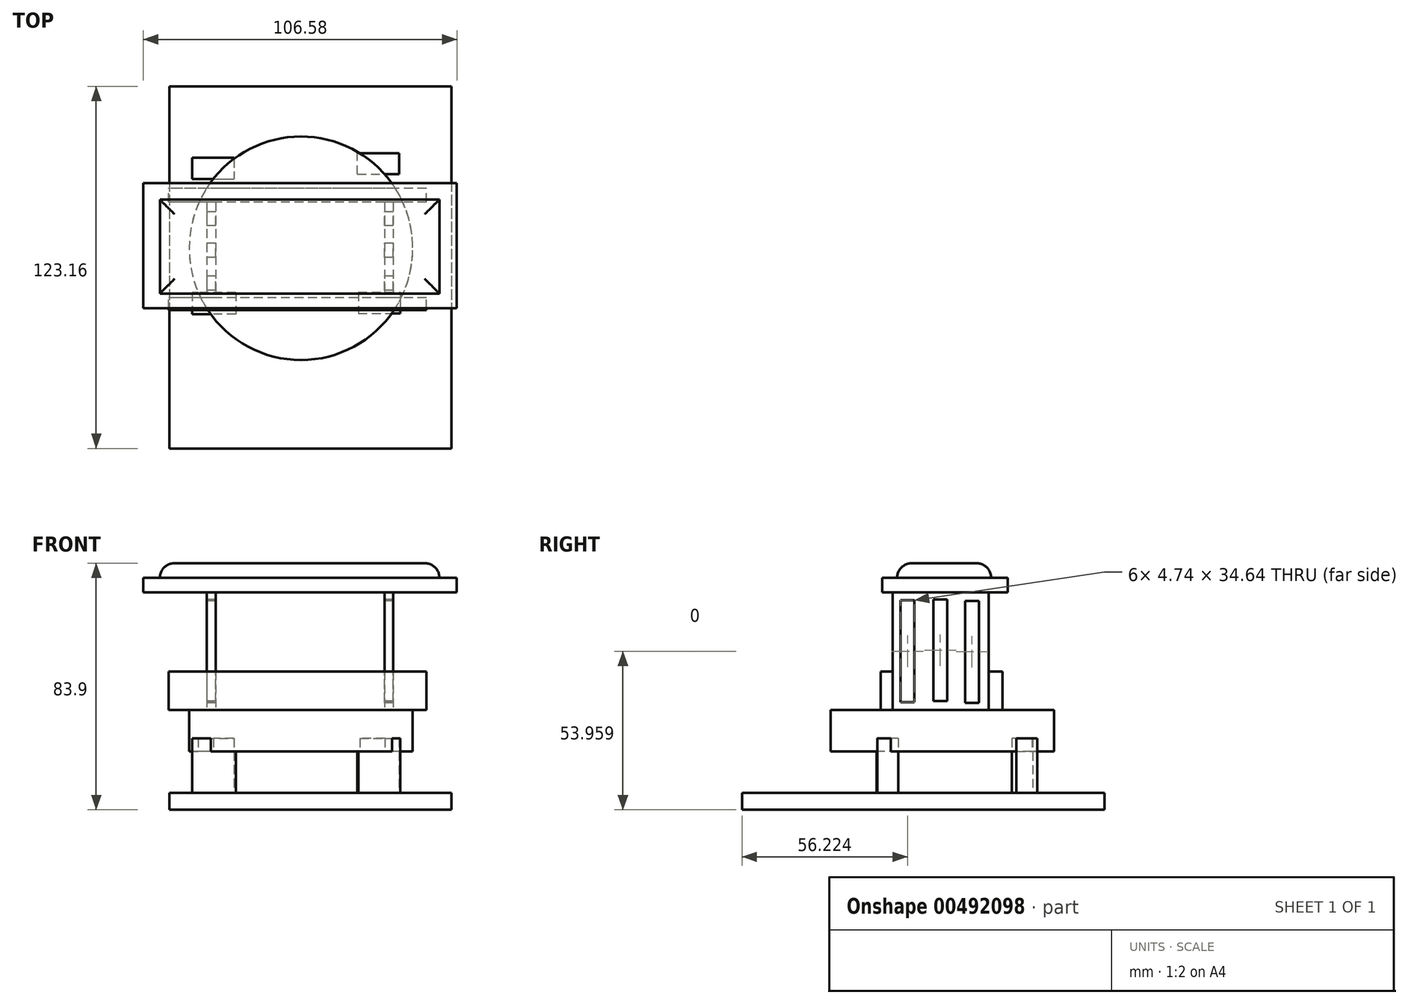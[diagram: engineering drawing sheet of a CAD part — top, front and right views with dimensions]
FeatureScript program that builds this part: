
annotation { "Feature Type Name" : "Feature", "Feature Type Description" : "" }
export const myFeature = defineFeature(function(context is Context, id is Id, definition is map)
    precondition{}
    {
        {
            var Q0;
            Q0=qCreatedBy(makeId("Top.planeOp"),FACE);
            var sketch = newSketch(context, id + "F0", { "sketchPlane" : qUnion([Q0])});
            skLineSegment(sketch, "E0.bottom", {"start": v(-47.96, 61.58) * mm, "end": v(47.96, 61.58) * mm});
            skLineSegment(sketch, "E0.top", {"start": v(-47.96, -61.58) * mm, "end": v(47.96, -61.58) * mm});
            skLineSegment(sketch, "E0.left", {"start": v(-47.96, 61.58) * mm, "end": v(-47.96, -61.58) * mm});
            skLineSegment(sketch, "E0.right", {"start": v(47.96, 61.58) * mm, "end": v(47.96, -61.58) * mm});
            skPoint(sketch, "E0.middle", {"position": v(0, 0) * mm});
            skSolve(sketch);
        }
        {
            var Q0;
            Q0=makeQuery(id+"F0.imprint","IMPRINT",FACE,{"disambiguationData":[TD([[makeQuery(id+"F0.imprint","IMPRINT",EDGE,{"derivedFrom":sQuery(id+"F0.wireOp",EDGE,"E0.bottom")}),-1.0]])]});
            extrude(context, id + "F1", {"entities" : qUnion([Q0]), "depth" : 5.8 * mm});
        }
        {
            var Q0;
            Q0=makeQuery(id+"F1.opExtrude","CAP_FACE",FACE,{"disambiguationData":[OSD([sQuery(id+"F0.wireOp",EDGE,"E0.bottom"),sQuery(id+"F0.wireOp",EDGE,"E0.top"),sQuery(id+"F0.wireOp",EDGE,"E0.left"),sQuery(id+"F0.wireOp",EDGE,"E0.right")])],"isStart":false});
            var sketch = newSketch(context, id + "F2", { "sketchPlane" : qUnion([Q0])});
            skLineSegment(sketch, "E1.bottom", {"start": v(-25.44, -8.5) * mm, "end": v(-40.27, -8.5) * mm});
            skLineSegment(sketch, "E1.top", {"start": v(-25.44, -15.91) * mm, "end": v(-40.27, -15.91) * mm});
            skLineSegment(sketch, "E1.left", {"start": v(-25.44, -8.5) * mm, "end": v(-25.44, -15.91) * mm});
            skLineSegment(sketch, "E1.right", {"start": v(-40.27, -8.5) * mm, "end": v(-40.27, -15.91) * mm});
            skPoint(sketch, "E1.middle", {"position": v(-32.86, -12.2) * mm});
            skLineSegment(sketch, "E2.bottom", {"start": v(-40.27, 37.26) * mm, "end": v(-26.06, 37.26) * mm});
            skLineSegment(sketch, "E2.top", {"start": v(-40.27, 30.12) * mm, "end": v(-26.06, 30.12) * mm});
            skLineSegment(sketch, "E2.left", {"start": v(-40.27, 37.26) * mm, "end": v(-40.27, 30.12) * mm});
            skLineSegment(sketch, "E2.right", {"start": v(-26.06, 37.26) * mm, "end": v(-26.06, 30.12) * mm});
            skPoint(sketch, "E2.middle", {"position": v(-33.17, 33.7) * mm});
            skLineSegment(sketch, "E3.bottom", {"start": v(15.96, 31.67) * mm, "end": v(30.17, 31.67) * mm});
            skLineSegment(sketch, "E3.top", {"start": v(15.96, 38.8) * mm, "end": v(30.17, 38.8) * mm});
            skLineSegment(sketch, "E3.left", {"start": v(15.96, 31.67) * mm, "end": v(15.96, 38.8) * mm});
            skLineSegment(sketch, "E3.right", {"start": v(30.17, 31.67) * mm, "end": v(30.17, 38.8) * mm});
            skPoint(sketch, "E3.middle", {"position": v(23.06, 35.24) * mm});
            skLineSegment(sketch, "E4.bottom", {"start": v(16.26, -8.46) * mm, "end": v(30.48, -8.46) * mm});
            skLineSegment(sketch, "E4.top", {"start": v(16.26, -15.6) * mm, "end": v(30.48, -15.6) * mm});
            skLineSegment(sketch, "E4.left", {"start": v(16.26, -8.46) * mm, "end": v(16.26, -15.6) * mm});
            skLineSegment(sketch, "E4.right", {"start": v(30.48, -8.46) * mm, "end": v(30.48, -15.6) * mm});
            skPoint(sketch, "E4.middle", {"position": v(23.37, -12.03) * mm});
            skSolve(sketch);
        }
        {
            var Q0;
            Q0=makeQuery(id+"F2.imprint","IMPRINT",FACE,{"disambiguationData":[TD([[makeQuery(id+"F2.imprint","IMPRINT",EDGE,{"derivedFrom":sQuery(id+"F2.wireOp",EDGE,"E2.bottom")}),-1.0]])]});
            var Q1;
            Q1=makeQuery(id+"F2.imprint","IMPRINT",FACE,{"disambiguationData":[TD([[makeQuery(id+"F2.imprint","IMPRINT",EDGE,{"derivedFrom":sQuery(id+"F2.wireOp",EDGE,"E3.bottom")}),1.0]])]});
            var Q2;
            Q2=makeQuery(id+"F2.imprint","IMPRINT",FACE,{"disambiguationData":[TD([[makeQuery(id+"F2.imprint","IMPRINT",EDGE,{"derivedFrom":sQuery(id+"F2.wireOp",EDGE,"E4.bottom")}),-1.0]])]});
            var Q3;
            Q3=makeQuery(id+"F2.imprint","IMPRINT",FACE,{"disambiguationData":[TD([[makeQuery(id+"F2.imprint","IMPRINT",EDGE,{"derivedFrom":sQuery(id+"F2.wireOp",EDGE,"E1.bottom")}),1.0]])]});
            extrude(context, id + "F3", {"entities" : qUnion([Q0, Q1, Q2, Q3]), "operationType" : NewBodyOperationType.ADD, "depth" : 18.5 * mm});
        }
        {
            var Q0;
            Q0=makeQuery(id+"F3.opExtrude","CAP_FACE",FACE,{"disambiguationData":[OSD([sQuery(id+"F2.wireOp",EDGE,"E2.bottom"),sQuery(id+"F2.wireOp",EDGE,"E2.top"),sQuery(id+"F2.wireOp",EDGE,"E2.left"),sQuery(id+"F2.wireOp",EDGE,"E2.right")])],"isStart":false});
            cPlane(context, id + "F4", {"entities" : qUnion([Q0]), "cplaneType" : CPlaneType.OFFSET, "offset" : 4.4 * mm, "oppositeDirection" : true, "width" : 150 * mm, "height" : 150 * mm});
        }
        {
            var Q0;
            Q0=qCreatedBy(id+"F4.planeOp",FACE);
            var sketch = newSketch(context, id + "F5", { "sketchPlane" : qUnion([Q0])});
            skCircle(sketch, "E5", {"center": v(-3.26, 6.51) * mm, "radius": 38 * mm});
            skSolve(sketch);
        }
        {
            var Q0;
            Q0 = qSketchRegion(id + "F5", true);
            extrude(context, id + "F6", {"entities" : qUnion([Q0]), "operationType" : NewBodyOperationType.ADD, "depth" : 14 * mm});
        }
        {
            var Q0;
            Q0=makeQuery(id+"F6.opExtrude","CAP_FACE",FACE,{"disambiguationData":[OSD([sQuery(id+"F5.wireOp",EDGE,"E5")])],"isStart":false});
            var sketch = newSketch(context, id + "F7", { "sketchPlane" : qUnion([Q0])});
            skLineSegment(sketch, "E6.bottom", {"start": v(39.38, 22.2) * mm, "end": v(-48.26, 22.2) * mm});
            skLineSegment(sketch, "E6.top", {"start": v(39.38, 26.94) * mm, "end": v(-48.26, 26.94) * mm});
            skLineSegment(sketch, "E6.left", {"start": v(39.38, 22.2) * mm, "end": v(39.38, 26.94) * mm});
            skLineSegment(sketch, "E6.right", {"start": v(-48.26, 22.2) * mm, "end": v(-48.26, 26.94) * mm});
            skPoint(sketch, "E6.middle", {"position": v(-4.44, 24.57) * mm});
            skLineSegment(sketch, "E7.bottom", {"start": v(39.38, -14.5) * mm, "end": v(-48.26, -14.5) * mm});
            skLineSegment(sketch, "E7.top", {"start": v(39.38, -10.36) * mm, "end": v(-48.26, -10.36) * mm});
            skLineSegment(sketch, "E7.left", {"start": v(39.38, -14.5) * mm, "end": v(39.38, -10.36) * mm});
            skLineSegment(sketch, "E7.right", {"start": v(-48.26, -14.5) * mm, "end": v(-48.26, -10.36) * mm});
            skPoint(sketch, "E7.middle", {"position": v(-4.44, -12.43) * mm});
            skSolve(sketch);
        }
        {
            var Q0;
            {var subQ0=sQuery(id+"F7.wireOp",EDGE,"E7.bottom");var subQ1=makeQuery(id+"F6.opExtrude","CAP_EDGE",EDGE,{"disambiguationData":[OSD([sQuery(id+"F5.wireOp",EDGE,"E5")])],"isStart":false});var subQ2=makeQuery(id+"F7.imprint","INTERSECT",VERTEX,{"disambiguationData":[OD(0.0)],"derivedFrom":[subQ1,subQ0]});Q0=makeQuery(id+"F7.imprint","IMPRINT",FACE,{"disambiguationData":[TD([[makeQuery(id+"F7.imprint","IMPRINT",EDGE,{"disambiguationData":[TD([[subQ2,-1.0]])],"derivedFrom":subQ0}),-1.0]])]});}
            var Q1;
            {var subQ0=sQuery(id+"F7.wireOp",EDGE,"E7.left");Q1=makeQuery(id+"F7.imprint","IMPRINT",FACE,{"disambiguationData":[TD([[makeQuery(id+"F7.imprint","IMPRINT",EDGE,{"derivedFrom":subQ0}),1.0]])]});}
            var Q2;
            {var subQ0=sQuery(id+"F7.wireOp",EDGE,"E7.right");Q2=makeQuery(id+"F7.imprint","IMPRINT",FACE,{"disambiguationData":[TD([[makeQuery(id+"F7.imprint","IMPRINT",EDGE,{"derivedFrom":subQ0}),-1.0]])]});}
            var Q3;
            {var subQ0=sQuery(id+"F7.wireOp",EDGE,"E6.bottom");var subQ1=makeQuery(id+"F6.opExtrude","CAP_EDGE",EDGE,{"disambiguationData":[OSD([sQuery(id+"F5.wireOp",EDGE,"E5")])],"isStart":false});var subQ2=makeQuery(id+"F7.imprint","INTERSECT",VERTEX,{"disambiguationData":[OD(0.0)],"derivedFrom":[subQ1,subQ0]});Q3=makeQuery(id+"F7.imprint","IMPRINT",FACE,{"disambiguationData":[TD([[makeQuery(id+"F7.imprint","IMPRINT",EDGE,{"disambiguationData":[TD([[subQ2,-1.0]])],"derivedFrom":subQ0}),-1.0]])]});}
            var Q4;
            {var subQ0=sQuery(id+"F7.wireOp",EDGE,"E6.right");Q4=makeQuery(id+"F7.imprint","IMPRINT",FACE,{"disambiguationData":[TD([[makeQuery(id+"F7.imprint","IMPRINT",EDGE,{"derivedFrom":subQ0}),-1.0]])]});}
            var Q5;
            {var subQ0=sQuery(id+"F7.wireOp",EDGE,"E6.left");Q5=makeQuery(id+"F7.imprint","IMPRINT",FACE,{"disambiguationData":[TD([[makeQuery(id+"F7.imprint","IMPRINT",EDGE,{"derivedFrom":subQ0}),1.0]])]});}
            extrude(context, id + "F8", {"entities" : qUnion([Q0, Q1, Q2, Q3, Q4, Q5]), "operationType" : NewBodyOperationType.ADD, "depth" : 13.2 * mm});
        }
        {
            var Q0;
            {var subQ1=sQuery(id+"F7.wireOp",EDGE,"E6.bottom");var subQ2=sQuery(id+"F5.wireOp",EDGE,"E5");Q0=makeQuery(id+"F8.boolean.opBoolean","SPLIT",FACE,{"disambiguationData":[TD([makeQuery(id+"F8.opExtrude","SWEPT_FACE",FACE,{"disambiguationData":[OSD([subQ1])]})])],"derivedFrom":makeQuery(id+"F6.opExtrude","CAP_FACE",FACE,{"disambiguationData":[OSD([subQ2])],"isStart":false})});}
            var sketch = newSketch(context, id + "F9", { "sketchPlane" : qUnion([Q0])});
            skLineSegment(sketch, "E8.bottom", {"start": v(-35.23, 22.2) * mm, "end": v(-32.27, 22.2) * mm});
            skLineSegment(sketch, "E8.top", {"start": v(-35.23, -10.36) * mm, "end": v(-32.27, -10.36) * mm});
            skLineSegment(sketch, "E8.left", {"start": v(-35.23, 22.2) * mm, "end": v(-35.23, -10.36) * mm});
            skLineSegment(sketch, "E8.right", {"start": v(-32.27, 22.2) * mm, "end": v(-32.27, -10.36) * mm});
            skLineSegment(sketch, "E9.bottom", {"start": v(25.16, 22.2) * mm, "end": v(28.12, 22.2) * mm});
            skLineSegment(sketch, "E9.top", {"start": v(25.16, -10.36) * mm, "end": v(28.12, -10.36) * mm});
            skLineSegment(sketch, "E9.left", {"start": v(25.16, 22.2) * mm, "end": v(25.16, -10.36) * mm});
            skLineSegment(sketch, "E9.right", {"start": v(28.12, 22.2) * mm, "end": v(28.12, -10.36) * mm});
            skSolve(sketch);
        }
        {
            var Q0;
            Q0=makeQuery(id+"F9.imprint","IMPRINT",FACE,{"disambiguationData":[TD([[makeQuery(id+"F9.imprint","IMPRINT",EDGE,{"derivedFrom":sQuery(id+"F9.wireOp",EDGE,"E8.bottom")}),1.0]])]});
            var Q1;
            Q1=makeQuery(id+"F9.imprint","IMPRINT",FACE,{"disambiguationData":[TD([[makeQuery(id+"F9.imprint","IMPRINT",EDGE,{"derivedFrom":sQuery(id+"F9.wireOp",EDGE,"E9.bottom")}),1.0]])]});
            extrude(context, id + "F10", {"entities" : qUnion([Q0, Q1]), "operationType" : NewBodyOperationType.ADD, "depth" : 40 * mm});
        }
        {
            var Q0;
            Q0=makeQuery(id+"F10.opExtrude","CAP_FACE",FACE,{"disambiguationData":[OSD([sQuery(id+"F9.wireOp",EDGE,"E9.bottom"),sQuery(id+"F9.wireOp",EDGE,"E9.top"),sQuery(id+"F9.wireOp",EDGE,"E9.left"),sQuery(id+"F9.wireOp",EDGE,"E9.right")])],"isStart":false});
            cPlane(context, id + "F11", {"entities" : qUnion([Q0]), "cplaneType" : CPlaneType.OFFSET, "offset" : 0 * mm, "width" : 150 * mm, "height" : 150 * mm});
        }
        {
            var Q0;
            Q0=qCreatedBy(id+"F11.planeOp",FACE);
            var sketch = newSketch(context, id + "F12", { "sketchPlane" : qUnion([Q0])});
            skLineSegment(sketch, "E10.bottom", {"start": v(-56.84, 28.72) * mm, "end": v(49.74, 28.72) * mm});
            skLineSegment(sketch, "E10.top", {"start": v(-56.84, -13.91) * mm, "end": v(49.74, -13.91) * mm});
            skLineSegment(sketch, "E10.left", {"start": v(-56.84, 28.72) * mm, "end": v(-56.84, -13.91) * mm});
            skLineSegment(sketch, "E10.right", {"start": v(49.74, 28.72) * mm, "end": v(49.74, -13.91) * mm});
            skPoint(sketch, "E10.middle", {"position": v(-3.55, 7.4) * mm});
            skSolve(sketch);
        }
        {
            var Q0;
            Q0=makeQuery(id+"F12.imprint","IMPRINT",FACE,{"disambiguationData":[TD([[makeQuery(id+"F12.imprint","IMPRINT",EDGE,{"derivedFrom":sQuery(id+"F12.wireOp",EDGE,"E10.bottom")}),-1.0]])]});
            extrude(context, id + "F13", {"entities" : qUnion([Q0]), "operationType" : NewBodyOperationType.ADD, "depth" : 5 * mm});
        }
        {
            var Q0;
            Q0=makeQuery(id+"F13.opExtrude","CAP_FACE",FACE,{"disambiguationData":[OSD([sQuery(id+"F12.wireOp",EDGE,"E10.bottom"),sQuery(id+"F12.wireOp",EDGE,"E10.top"),sQuery(id+"F12.wireOp",EDGE,"E10.left"),sQuery(id+"F12.wireOp",EDGE,"E10.right")])],"isStart":false});
            var sketch = newSketch(context, id + "F14", { "sketchPlane" : qUnion([Q0])});
            skSolve(sketch);
        }
        {
            var Q0;
            Q0=makeQuery(id+"F14.imprint","IMPRINT",FACE,{"disambiguationData":[TD([[makeQuery(id+"F14.imprint","IMPRINT",EDGE,{"derivedFrom":makeQuery(id+"F13.opExtrude","CAP_EDGE",EDGE,{"disambiguationData":[OSD([sQuery(id+"F12.wireOp",EDGE,"E10.bottom")])],"isStart":false})}),-1.0]])]});
            var sketch = newSketch(context, id + "F15", { "sketchPlane" : qUnion([Q0])});
            skLineSegment(sketch, "E11.bottom", {"start": v(-51.22, 23.1) * mm, "end": v(43.82, 23.1) * mm});
            skLineSegment(sketch, "E11.top", {"start": v(-51.22, -8.88) * mm, "end": v(43.82, -8.88) * mm});
            skLineSegment(sketch, "E11.left", {"start": v(-51.22, 23.1) * mm, "end": v(-51.22, -8.88) * mm});
            skLineSegment(sketch, "E11.right", {"start": v(43.82, 23.1) * mm, "end": v(43.82, -8.88) * mm});
            skSolve(sketch);
        }
        {
            var Q0;
            Q0=makeQuery(id+"F15.imprint","IMPRINT",FACE,{"disambiguationData":[TD([[makeQuery(id+"F15.imprint","IMPRINT",EDGE,{"derivedFrom":sQuery(id+"F15.wireOp",EDGE,"E11.bottom")}),-1.0]])]});
            extrude(context, id + "F16", {"entities" : qUnion([Q0]), "operationType" : NewBodyOperationType.ADD, "depth" : 5 * mm});
        }
        {
            var Q0;
            Q0=makeQuery(id+"F16.opExtrude","CAP_EDGE",EDGE,{"disambiguationData":[OSD([sQuery(id+"F15.wireOp",EDGE,"E11.bottom")])],"isStart":false});
            var Q1;
            Q1=makeQuery(id+"F16.opExtrude","CAP_EDGE",EDGE,{"disambiguationData":[OSD([sQuery(id+"F15.wireOp",EDGE,"E11.left")])],"isStart":false});
            var Q2;
            Q2=makeQuery(id+"F16.opExtrude","CAP_EDGE",EDGE,{"disambiguationData":[OSD([sQuery(id+"F15.wireOp",EDGE,"E11.top")])],"isStart":false});
            var Q3;
            Q3=makeQuery(id+"F16.opExtrude","CAP_EDGE",EDGE,{"disambiguationData":[OSD([sQuery(id+"F15.wireOp",EDGE,"E11.right")])],"isStart":false});
            fillet(context, id + "F17", {"entities" : qUnion([Q0, Q1, Q2, Q3]), "radius" : 5 * mm, "tangentPropagation" : true, "allowEdgeOverflow" : false});
        }
        {
            var Q0;
            Q0=makeQuery(id+"F10.opExtrude","SWEPT_FACE",FACE,{"disambiguationData":[OSD([sQuery(id+"F9.wireOp",EDGE,"E8.left")])]});
            var sketch = newSketch(context, id + "F18", { "sketchPlane" : qUnion([Q0])});
            skLineSegment(sketch, "E12.bottom", {"start": v(-18.95, 71.06) * mm, "end": v(-14.21, 71.06) * mm});
            skLineSegment(sketch, "E12.top", {"start": v(-18.95, 36.42) * mm, "end": v(-14.21, 36.42) * mm});
            skLineSegment(sketch, "E12.left", {"start": v(-18.95, 71.06) * mm, "end": v(-18.95, 36.42) * mm});
            skLineSegment(sketch, "E12.right", {"start": v(-14.21, 71.06) * mm, "end": v(-14.21, 36.42) * mm});
            skSolve(sketch);
        }
        {
            var Q0;
            Q0=makeQuery(id+"F18.imprint","IMPRINT",FACE,{"disambiguationData":[TD([[makeQuery(id+"F18.imprint","IMPRINT",EDGE,{"derivedFrom":sQuery(id+"F18.wireOp",EDGE,"E12.bottom")}),-1.0]])]});
            extrude(context, id + "F19", {"entities" : qUnion([Q0]), "operationType" : NewBodyOperationType.REMOVE, "oppositeDirection" : true, "depth" : 69.8 * mm});
        }
        {
            var Q0;
            Q0=makeQuery(id+"F10.opExtrude","SWEPT_FACE",FACE,{"disambiguationData":[OSD([sQuery(id+"F9.wireOp",EDGE,"E8.left")])]});
            var sketch = newSketch(context, id + "F20", { "sketchPlane" : qUnion([Q0])});
            skLineSegment(sketch, "E13.bottom", {"start": v(-8.17, 71.59) * mm, "end": v(-3.43, 71.59) * mm});
            skLineSegment(sketch, "E13.top", {"start": v(-8.17, 36.95) * mm, "end": v(-3.43, 36.95) * mm});
            skLineSegment(sketch, "E13.left", {"start": v(-8.17, 71.59) * mm, "end": v(-8.17, 36.95) * mm});
            skLineSegment(sketch, "E13.right", {"start": v(-3.43, 71.59) * mm, "end": v(-3.43, 36.95) * mm});
            skSolve(sketch);
        }
        {
            var Q0;
            Q0=makeQuery(id+"F20.imprint","IMPRINT",FACE,{"disambiguationData":[TD([[makeQuery(id+"F20.imprint","IMPRINT",EDGE,{"derivedFrom":sQuery(id+"F20.wireOp",EDGE,"E13.bottom")}),-1.0]])]});
            extrude(context, id + "F21", {"entities" : qUnion([Q0]), "operationType" : NewBodyOperationType.REMOVE, "oppositeDirection" : true, "depth" : 93.3 * mm});
        }
        {
            var Q0;
            Q0=makeQuery(id+"F10.opExtrude","SWEPT_FACE",FACE,{"disambiguationData":[OSD([sQuery(id+"F9.wireOp",EDGE,"E8.left")])]});
            var sketch = newSketch(context, id + "F22", { "sketchPlane" : qUnion([Q0])});
            skLineSegment(sketch, "E14.bottom", {"start": v(2.99, 71.28) * mm, "end": v(7.72, 71.28) * mm});
            skLineSegment(sketch, "E14.top", {"start": v(2.99, 36.64) * mm, "end": v(7.72, 36.64) * mm});
            skLineSegment(sketch, "E14.left", {"start": v(2.99, 71.28) * mm, "end": v(2.99, 36.64) * mm});
            skLineSegment(sketch, "E14.right", {"start": v(7.72, 71.28) * mm, "end": v(7.72, 36.64) * mm});
            skSolve(sketch);
        }
        {
            var Q0;
            Q0=makeQuery(id+"F22.imprint","IMPRINT",FACE,{"disambiguationData":[TD([[makeQuery(id+"F22.imprint","IMPRINT",EDGE,{"derivedFrom":sQuery(id+"F22.wireOp",EDGE,"E14.bottom")}),-1.0]])]});
            extrude(context, id + "F23", {"entities" : qUnion([Q0]), "operationType" : NewBodyOperationType.REMOVE, "oppositeDirection" : true, "depth" : 98.3 * mm});
        }
    });
